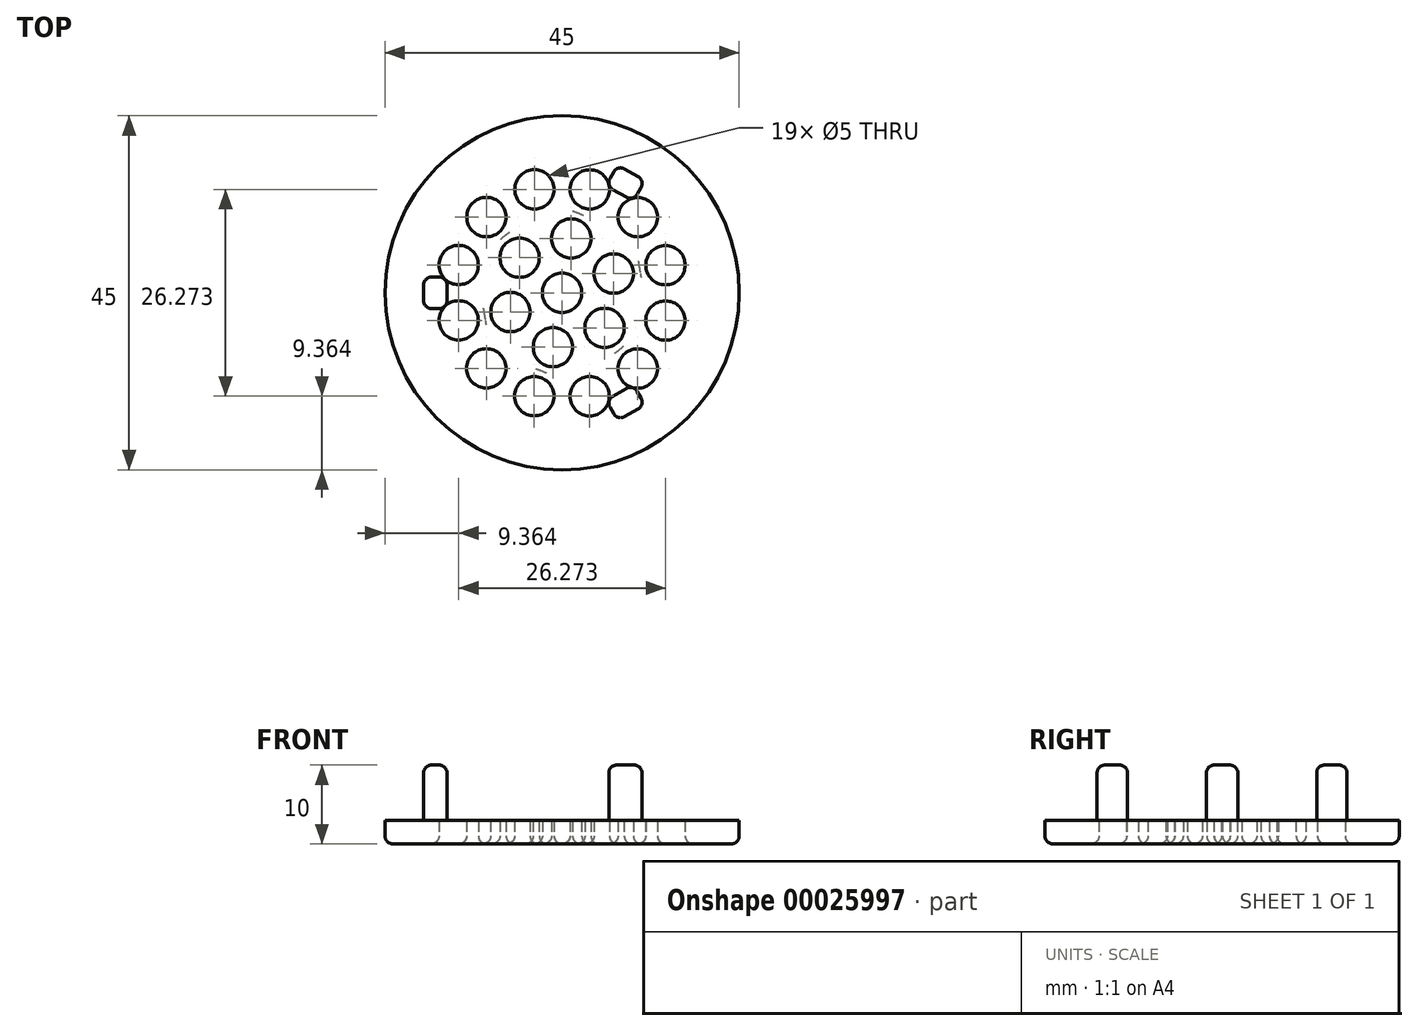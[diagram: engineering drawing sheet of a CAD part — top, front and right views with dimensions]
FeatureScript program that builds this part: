
annotation { "Feature Type Name" : "Feature", "Feature Type Description" : "" }
export const myFeature = defineFeature(function(context is Context, id is Id, definition is map)
    precondition{}
    {
        {
            var Q0;
            Q0=qCreatedBy(makeId("Top.planeOp"),FACE);
            var sketch = newSketch(context, id + "F0", { "sketchPlane" : qUnion([Q0])});
            skCircle(sketch, "E0", {"center": v(0, 0) * mm, "radius": 22.5 * mm});
            skCircle(sketch, "E1", {"center": v(-5.4, 4.46) * mm, "radius": 2.5 * mm});
            skCircle(sketch, "E2.1.0", {"center": v(-6.56, -2.44) * mm, "radius": 2.5 * mm});
            skCircle(sketch, "E2.2.0", {"center": v(-1.17, -6.9) * mm, "radius": 2.5 * mm});
            skCircle(sketch, "E2.3.0", {"center": v(5.4, -4.46) * mm, "radius": 2.5 * mm});
            skCircle(sketch, "E2.4.0", {"center": v(6.56, 2.44) * mm, "radius": 2.5 * mm});
            skCircle(sketch, "E3", {"center": v(0, 0) * mm, "radius": 2.5 * mm});
            skCircle(sketch, "E4.1.5.0", {"center": v(1.17, 6.9) * mm, "radius": 2.5 * mm});
            skCircle(sketch, "E5", {"center": v(-3.5, 13.14) * mm, "radius": 2.5 * mm});
            skCircle(sketch, "E6.1.0", {"center": v(-9.6, 9.62) * mm, "radius": 2.5 * mm});
            skCircle(sketch, "E6.2.0", {"center": v(-13.13, 3.53) * mm, "radius": 2.5 * mm});
            skCircle(sketch, "E6.3.0", {"center": v(-13.14, -3.5) * mm, "radius": 2.5 * mm});
            skCircle(sketch, "E6.4.0", {"center": v(-9.62, -9.6) * mm, "radius": 2.5 * mm});
            skCircle(sketch, "E6.5.0", {"center": v(-3.53, -13.13) * mm, "radius": 2.5 * mm});
            skCircle(sketch, "E6.6.0", {"center": v(3.5, -13.14) * mm, "radius": 2.5 * mm});
            skCircle(sketch, "E6.7.0", {"center": v(9.6, -9.62) * mm, "radius": 2.5 * mm});
            skCircle(sketch, "E6.8.0", {"center": v(13.13, -3.53) * mm, "radius": 2.5 * mm});
            skCircle(sketch, "E6.9.0", {"center": v(13.14, 3.5) * mm, "radius": 2.5 * mm});
            skCircle(sketch, "E6.10.0", {"center": v(9.62, 9.6) * mm, "radius": 2.5 * mm});
            skCircle(sketch, "E7.0.11.0", {"center": v(3.53, 13.13) * mm, "radius": 2.5 * mm});
            skSolve(sketch);
        }
        {
            var Q0;
            Q0 = qSketchRegion(id + "F0", true);
            extrude(context, id + "F1", {"entities" : qUnion([Q0]), "depth" : 3 * mm});
        }
        {
            var Q0;
            Q0=qCreatedBy(makeId("Top.planeOp"),FACE);
            var sketch = newSketch(context, id + "F2", { "sketchPlane" : qUnion([Q0])});
            skLineSegment(sketch, "E8.bottom", {"start": v(-16.6, 2) * mm, "end": v(-15.6, 2) * mm});
            skLineSegment(sketch, "E8.top", {"start": v(-16.6, -2) * mm, "end": v(-15.6, -2) * mm});
            skLineSegment(sketch, "E8.left", {"start": v(-17.6, 1) * mm, "end": v(-17.6, -1) * mm});
            skLineSegment(sketch, "E8.right", {"start": v(-14.6, 1) * mm, "end": v(-14.6, -1) * mm});
            skPoint(sketch, "E9.center", {"position": v(0, 0) * mm});
            skPoint(sketch, "E10.visualSharp", {"position": v(-17.6, 2) * mm});
            skArc(sketch, "E10.filletArc", {"start": v(-16.6, 2) * mm, "mid": v(-17.3, 1.7) * mm, "end": v(-17.6, 1) * mm});
            skPoint(sketch, "E11.visualSharp", {"position": v(-14.6, 2) * mm});
            skArc(sketch, "E11.filletArc", {"start": v(-14.6, 1) * mm, "mid": v(-14.9, 1.7) * mm, "end": v(-15.6, 2) * mm});
            skPoint(sketch, "E12.visualSharp", {"position": v(-14.6, -2) * mm});
            skArc(sketch, "E12.filletArc", {"start": v(-15.6, -2) * mm, "mid": v(-14.9, -1.7) * mm, "end": v(-14.6, -1) * mm});
            skPoint(sketch, "E13.visualSharp", {"position": v(-17.6, -2) * mm});
            skArc(sketch, "E13.filletArc", {"start": v(-17.6, -1) * mm, "mid": v(-17.3, -1.7) * mm, "end": v(-16.6, -2) * mm});
            skPoint(sketch, "E14.1.0", {"position": v(7.07, -16.24) * mm});
            skPoint(sketch, "E14.1.1", {"position": v(9.03, -11.64) * mm});
            skPoint(sketch, "E14.1.2", {"position": v(10.53, -14.24) * mm});
            skLineSegment(sketch, "E14.1.3", {"start": v(6.57, -15.38) * mm, "end": v(6.07, -14.5) * mm});
            skPoint(sketch, "E14.1.4", {"position": v(5.57, -13.64) * mm});
            skArc(sketch, "E14.1.5", {"start": v(9.53, -12.5) * mm, "mid": v(8.92, -12.04) * mm, "end": v(8.17, -12.14) * mm});
            skArc(sketch, "E14.1.6", {"start": v(6.57, -15.38) * mm, "mid": v(7.18, -15.84) * mm, "end": v(7.93, -15.74) * mm});
            skArc(sketch, "E14.1.7", {"start": v(6.43, -13.14) * mm, "mid": v(5.97, -13.75) * mm, "end": v(6.07, -14.5) * mm});
            skArc(sketch, "E14.1.8", {"start": v(9.67, -14.74) * mm, "mid": v(10.13, -14.13) * mm, "end": v(10.03, -13.38) * mm});
            skLineSegment(sketch, "E14.1.9", {"start": v(6.43, -13.14) * mm, "end": v(8.17, -12.14) * mm});
            skLineSegment(sketch, "E14.1.10", {"start": v(7.93, -15.74) * mm, "end": v(9.67, -14.74) * mm});
            skLineSegment(sketch, "E14.1.11", {"start": v(10.03, -13.38) * mm, "end": v(9.53, -12.5) * mm});
            skPoint(sketch, "E14.2.0", {"position": v(10.53, 14.24) * mm});
            skPoint(sketch, "E14.2.1", {"position": v(5.57, 13.64) * mm});
            skPoint(sketch, "E14.2.2", {"position": v(7.07, 16.24) * mm});
            skLineSegment(sketch, "E14.2.3", {"start": v(10.03, 13.38) * mm, "end": v(9.53, 12.5) * mm});
            skPoint(sketch, "E14.2.4", {"position": v(9.03, 11.64) * mm});
            skArc(sketch, "E14.2.5", {"start": v(6.07, 14.5) * mm, "mid": v(5.97, 13.75) * mm, "end": v(6.43, 13.14) * mm});
            skArc(sketch, "E14.2.6", {"start": v(10.03, 13.38) * mm, "mid": v(10.13, 14.13) * mm, "end": v(9.67, 14.74) * mm});
            skArc(sketch, "E14.2.7", {"start": v(8.17, 12.14) * mm, "mid": v(8.92, 12.04) * mm, "end": v(9.53, 12.5) * mm});
            skArc(sketch, "E14.2.8", {"start": v(7.93, 15.74) * mm, "mid": v(7.18, 15.84) * mm, "end": v(6.57, 15.38) * mm});
            skLineSegment(sketch, "E14.2.9", {"start": v(8.17, 12.14) * mm, "end": v(6.43, 13.14) * mm});
            skLineSegment(sketch, "E14.2.10", {"start": v(9.67, 14.74) * mm, "end": v(7.93, 15.74) * mm});
            skLineSegment(sketch, "E14.2.11", {"start": v(6.57, 15.38) * mm, "end": v(6.07, 14.5) * mm});
            skSolve(sketch);
        }
        {
            var Q0;
            Q0 = qSketchRegion(id + "F2", true);
            extrude(context, id + "F3", {"entities" : qUnion([Q0]), "operationType" : NewBodyOperationType.ADD, "depth" : 10 * mm});
        }
        {
            var Q0;
            Q0=makeQuery(id+"F1.opExtrude","CAP_FACE",FACE,{"disambiguationData":[OSD([sQuery(id+"F0.wireOp",EDGE,"E0"),sQuery(id+"F0.wireOp",EDGE,"E1"),sQuery(id+"F0.wireOp",EDGE,"E2.1.0"),sQuery(id+"F0.wireOp",EDGE,"E2.2.0"),sQuery(id+"F0.wireOp",EDGE,"E2.3.0"),sQuery(id+"F0.wireOp",EDGE,"E2.4.0"),sQuery(id+"F0.wireOp",EDGE,"E3"),sQuery(id+"F0.wireOp",EDGE,"E4.1.5.0"),sQuery(id+"F0.wireOp",EDGE,"E5"),sQuery(id+"F0.wireOp",EDGE,"E6.1.0"),sQuery(id+"F0.wireOp",EDGE,"E6.2.0"),sQuery(id+"F0.wireOp",EDGE,"E6.3.0"),sQuery(id+"F0.wireOp",EDGE,"E6.4.0"),sQuery(id+"F0.wireOp",EDGE,"E6.5.0"),sQuery(id+"F0.wireOp",EDGE,"E6.6.0"),sQuery(id+"F0.wireOp",EDGE,"E6.7.0"),sQuery(id+"F0.wireOp",EDGE,"E6.8.0"),sQuery(id+"F0.wireOp",EDGE,"E6.9.0"),sQuery(id+"F0.wireOp",EDGE,"E6.10.0"),sQuery(id+"F0.wireOp",EDGE,"E7.0.11.0")])],"isStart":true});
            fillet(context, id + "F4", {"entities" : qUnion([Q0]), "radius" : 1 * mm, "tangentPropagation" : true, "allowEdgeOverflow" : false});
        }
        {
            var Q0;
            Q0=makeQuery(id+"F3.opExtrude","CAP_FACE",FACE,{"disambiguationData":[OSD([sQuery(id+"F2.wireOp",EDGE,"E8.bottom"),sQuery(id+"F2.wireOp",EDGE,"E8.top"),sQuery(id+"F2.wireOp",EDGE,"E8.left"),sQuery(id+"F2.wireOp",EDGE,"E8.right"),sQuery(id+"F2.wireOp",EDGE,"E10.filletArc"),sQuery(id+"F2.wireOp",EDGE,"E11.filletArc"),sQuery(id+"F2.wireOp",EDGE,"E12.filletArc"),sQuery(id+"F2.wireOp",EDGE,"E13.filletArc")])],"isStart":false});
            var Q1;
            Q1=makeQuery(id+"F3.opExtrude","CAP_FACE",FACE,{"disambiguationData":[OSD([sQuery(id+"F2.wireOp",EDGE,"E14.2.3"),sQuery(id+"F2.wireOp",EDGE,"E14.2.5"),sQuery(id+"F2.wireOp",EDGE,"E14.2.6"),sQuery(id+"F2.wireOp",EDGE,"E14.2.7"),sQuery(id+"F2.wireOp",EDGE,"E14.2.8"),sQuery(id+"F2.wireOp",EDGE,"E14.2.9"),sQuery(id+"F2.wireOp",EDGE,"E14.2.10"),sQuery(id+"F2.wireOp",EDGE,"E14.2.11")])],"isStart":false});
            var Q2;
            Q2=makeQuery(id+"F3.opExtrude","CAP_FACE",FACE,{"disambiguationData":[OSD([sQuery(id+"F2.wireOp",EDGE,"E14.1.3"),sQuery(id+"F2.wireOp",EDGE,"E14.1.5"),sQuery(id+"F2.wireOp",EDGE,"E14.1.6"),sQuery(id+"F2.wireOp",EDGE,"E14.1.7"),sQuery(id+"F2.wireOp",EDGE,"E14.1.8"),sQuery(id+"F2.wireOp",EDGE,"E14.1.9"),sQuery(id+"F2.wireOp",EDGE,"E14.1.10"),sQuery(id+"F2.wireOp",EDGE,"E14.1.11")])],"isStart":false});
            fillet(context, id + "F5", {"entities" : qUnion([Q0, Q1, Q2]), "radius" : 1 * mm, "tangentPropagation" : true, "allowEdgeOverflow" : false});
        }
    });
